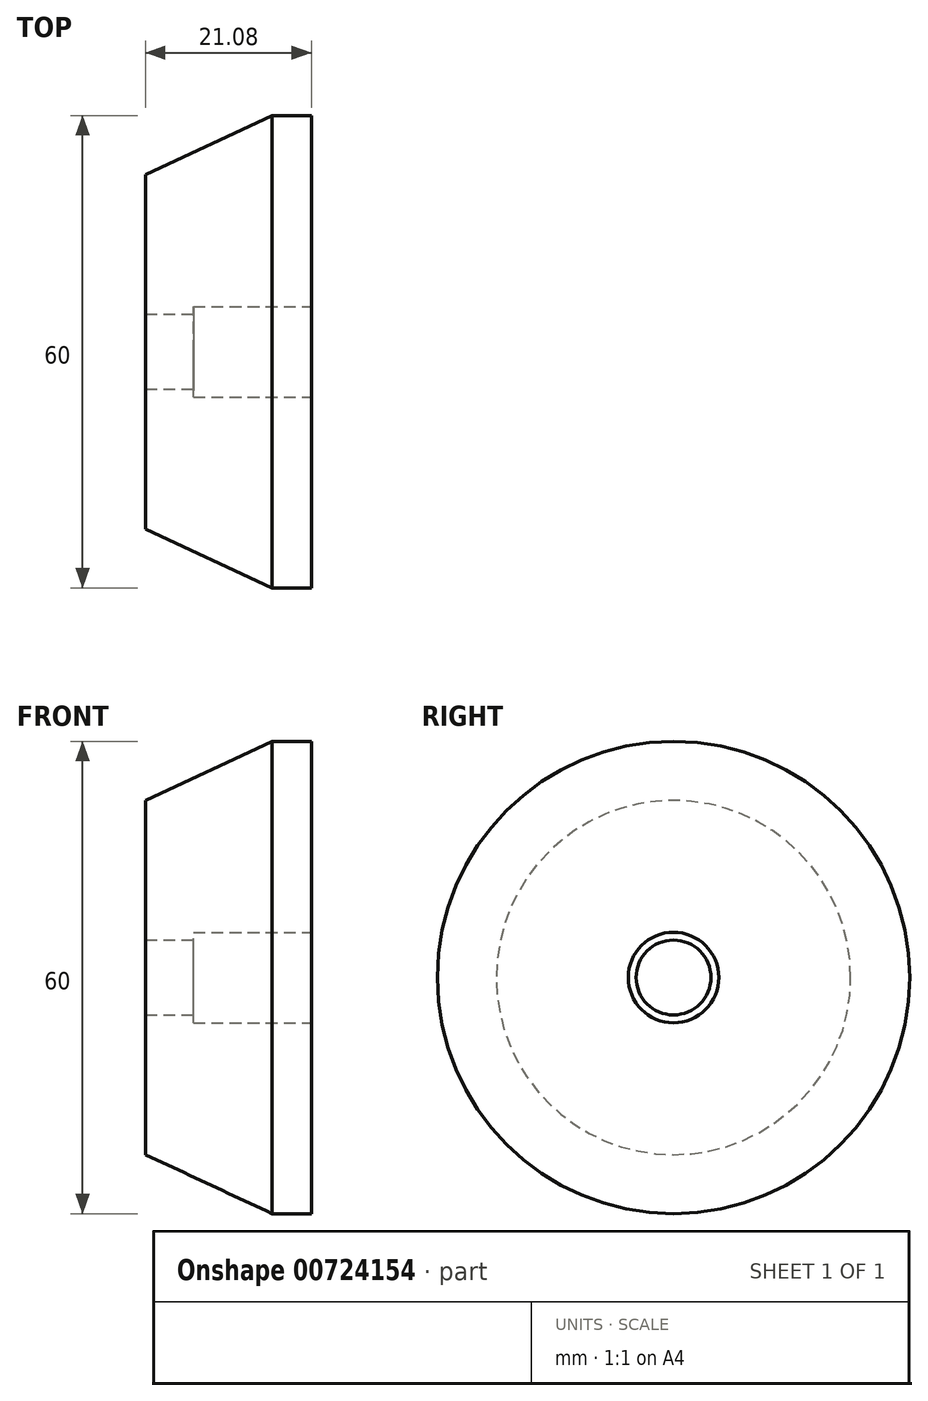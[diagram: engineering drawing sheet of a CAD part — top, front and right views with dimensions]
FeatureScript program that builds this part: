
annotation { "Feature Type Name" : "Feature", "Feature Type Description" : "" }
export const myFeature = defineFeature(function(context is Context, id is Id, definition is map)
    precondition{}
    {
        {
            var Q0;
            Q0=qCreatedBy(makeId("Front.planeOp"),FACE);
            var sketch = newSketch(context, id + "F0", { "sketchPlane" : qUnion([Q0])});
            skLineSegment(sketch, "E0", {"start": v(0, 0) * mm, "end": v(-23.81, 0) * mm, "construction": true});
            skLineSegment(sketch, "E1", {"start": v(0, 5.75) * mm, "end": v(0, 30) * mm});
            skLineSegment(sketch, "E2", {"start": v(0, 30) * mm, "end": v(-5, 30) * mm});
            skLineSegment(sketch, "E3", {"start": v(-5, 30) * mm, "end": v(-21.08, 22.5) * mm});
            skLineSegment(sketch, "E4", {"start": v(-21.08, 22.5) * mm, "end": v(-21.08, 5.75) * mm});
            skLineSegment(sketch, "E5", {"start": v(-15, 5.75) * mm, "end": v(0, 5.75) * mm});
            skLineSegment(sketch, "E6", {"start": v(-21.08, 5.75) * mm, "end": v(-21.08, 4.75) * mm});
            skLineSegment(sketch, "E7", {"start": v(-21.08, 4.75) * mm, "end": v(-15, 4.75) * mm});
            skLineSegment(sketch, "E8", {"start": v(-15, 4.75) * mm, "end": v(-15, 5.75) * mm});
            skSolve(sketch);
        }
        {
            var Q0;
            Q0=makeQuery(id+"F0.imprint","IMPRINT",FACE,{"disambiguationData":[TD([[makeQuery(id+"F0.imprint","IMPRINT",EDGE,{"derivedFrom":sQuery(id+"F0.wireOp",EDGE,"E1")}),1.0]])]});
            var Q1;
            Q1=sQuery(id+"F0.wireOp",EDGE,"E0");
            revolve(context, id + "F1", {"surfaceOperationType" : NewSurfaceOperationType.NEW, "entities" : qUnion([Q0]), "axis" : qUnion([Q1]), "revolveType" : RevolveType.FULL});
        }
    });
